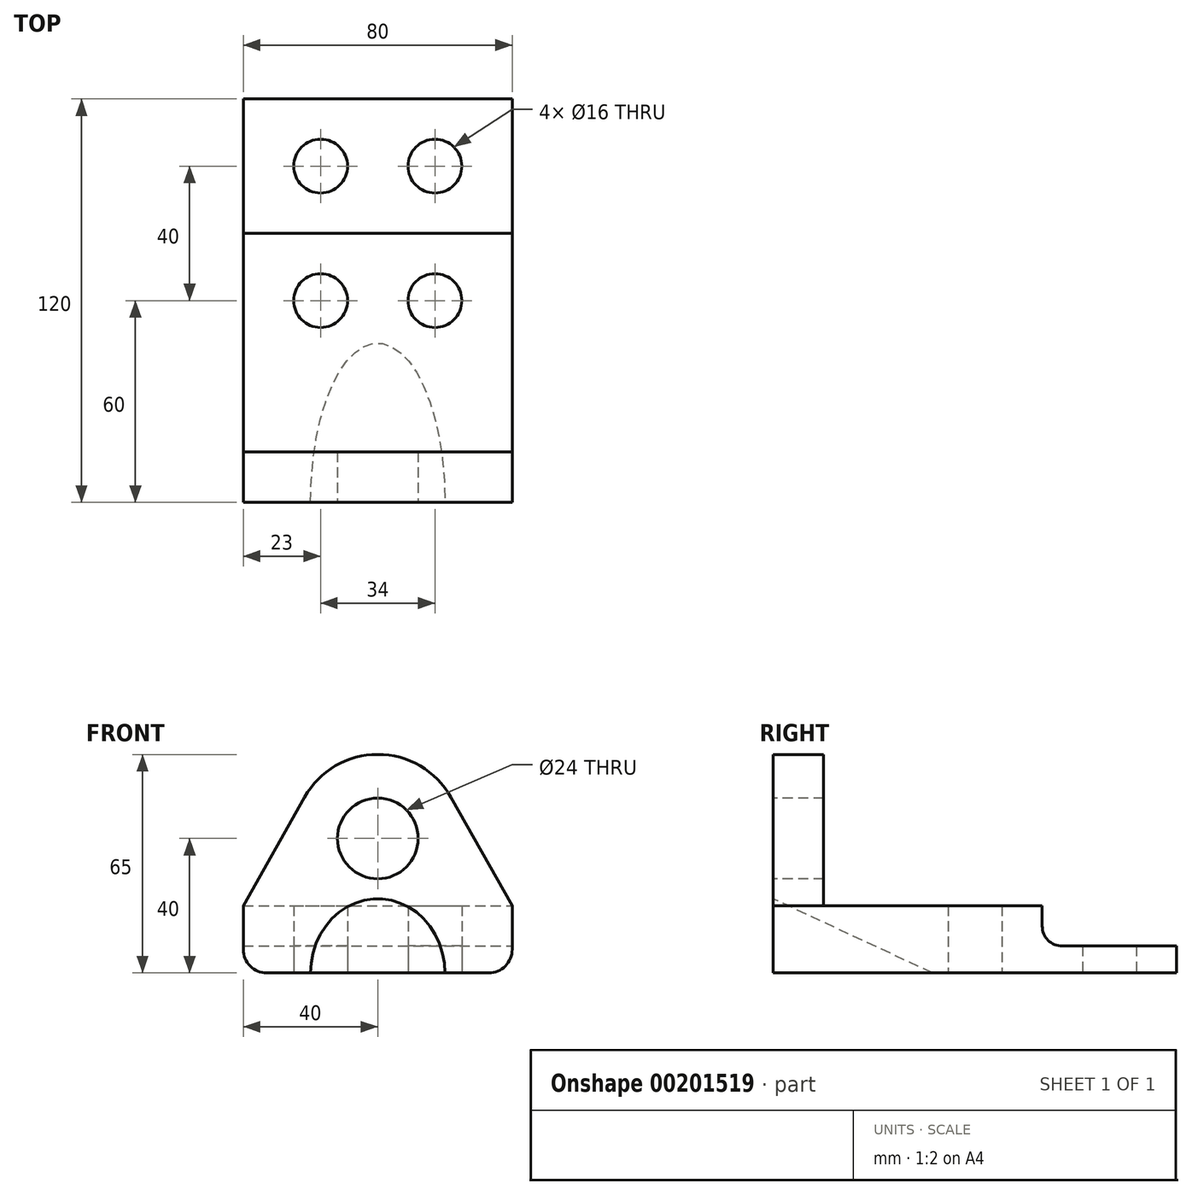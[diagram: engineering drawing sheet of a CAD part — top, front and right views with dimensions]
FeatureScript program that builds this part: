
annotation { "Feature Type Name" : "Feature", "Feature Type Description" : "" }
export const myFeature = defineFeature(function(context is Context, id is Id, definition is map)
    precondition{}
    {
        {
            var Q0;
            Q0=qCreatedBy(makeId("Front.planeOp"),FACE);
            var sketch = newSketch(context, id + "F0", { "sketchPlane" : qUnion([Q0])});
            skArc(sketch, "E0", {"start": v(21.77, 52.3) * mm, "mid": v(0, 65) * mm, "end": v(-21.77, 52.3) * mm});
            skLineSegment(sketch, "E1", {"start": v(-40, 0) * mm, "end": v(40, 0) * mm});
            skLineSegment(sketch, "E2", {"start": v(40, 0) * mm, "end": v(40, 20) * mm});
            skLineSegment(sketch, "E3", {"start": v(40, 20) * mm, "end": v(21.77, 52.3) * mm});
            skLineSegment(sketch, "E4", {"start": v(-40, 0) * mm, "end": v(-40, 20) * mm});
            skLineSegment(sketch, "E5", {"start": v(-40, 20) * mm, "end": v(-21.77, 52.3) * mm});
            skLineSegment(sketch, "E6", {"start": v(-40, 20) * mm, "end": v(40, 20) * mm});
            skCircle(sketch, "E7", {"center": v(0, 40) * mm, "radius": 12 * mm});
            skSolve(sketch);
        }
        {
            var Q0;
            Q0=makeQuery(id+"F0.imprint","IMPRINT",FACE,{"disambiguationData":[TD([[makeQuery(id+"F0.imprint","IMPRINT",EDGE,{"derivedFrom":sQuery(id+"F0.wireOp",EDGE,"E1")}),1.0]])]});
            extrude(context, id + "F1", {"entities" : qUnion([Q0]), "oppositeDirection" : true, "depth" : 120 * mm});
        }
        {
            var Q0;
            Q0=makeQuery(id+"F0.imprint","IMPRINT",FACE,{"disambiguationData":[TD([[makeQuery(id+"F0.imprint","IMPRINT",EDGE,{"derivedFrom":sQuery(id+"F0.wireOp",EDGE,"E0")}),1.0]])]});
            extrude(context, id + "F2", {"entities" : qUnion([Q0]), "operationType" : NewBodyOperationType.ADD, "oppositeDirection" : true, "depth" : 15 * mm});
        }
        {
            var Q0;
            Q0=makeQuery(id+"F1.opExtrude","SWEPT_FACE",FACE,{"disambiguationData":[OSD([sQuery(id+"F0.wireOp",EDGE,"E6")])]});
            var sketch = newSketch(context, id + "F3", { "sketchPlane" : qUnion([Q0])});
            skLineSegment(sketch, "E8.bottom", {"start": v(-40, 120) * mm, "end": v(40, 120) * mm});
            skLineSegment(sketch, "E8.top", {"start": v(-40, 80) * mm, "end": v(40, 80) * mm});
            skLineSegment(sketch, "E8.left", {"start": v(-40, 120) * mm, "end": v(-40, 80) * mm});
            skLineSegment(sketch, "E8.right", {"start": v(40, 120) * mm, "end": v(40, 80) * mm});
            skSolve(sketch);
        }
        {
            var Q0;
            Q0=makeQuery(id+"F3.imprint","IMPRINT",FACE,{"disambiguationData":[TD([[makeQuery(id+"F3.imprint","IMPRINT",EDGE,{"derivedFrom":sQuery(id+"F3.wireOp",EDGE,"E8.bottom")}),-1.0]])]});
            extrude(context, id + "F4", {"entities" : qUnion([Q0]), "operationType" : NewBodyOperationType.REMOVE, "oppositeDirection" : true, "depth" : (20 - 8) * mm});
        }
        {
            var Q0;
            Q0=makeQuery(id+"F4.boolean.opBoolean","COPY",EDGE,{"derivedFrom":makeQuery(id+"F4.opExtrude","CAP_EDGE",EDGE,{"disambiguationData":[OSD([sQuery(id+"F3.wireOp",EDGE,"E8.top")])],"isStart":false})});
            fillet(context, id + "F5", {"entities" : qUnion([Q0]), "radius" : 6 * mm, "tangentPropagation" : true, "allowEdgeOverflow" : false});
        }
        {
            var Q0;
            Q0=makeQuery(id+"F1.opExtrude","SWEPT_EDGE",EDGE,{"disambiguationData":[OSD([sQuery(id+"F0.wireOp",EDGE,"E1"),sQuery(id+"F0.wireOp",EDGE,"E2")])]});
            var Q1;
            Q1=makeQuery(id+"F1.opExtrude","SWEPT_EDGE",EDGE,{"disambiguationData":[OSD([sQuery(id+"F0.wireOp",EDGE,"E1"),sQuery(id+"F0.wireOp",EDGE,"E4")])]});
            fillet(context, id + "F6", {"entities" : qUnion([Q0, Q1]), "radius" : 7 * mm, "tangentPropagation" : true, "allowEdgeOverflow" : false});
        }
        {
            var Q0;
            Q0=makeQuery(id+"F1.opExtrude","SWEPT_FACE",FACE,{"disambiguationData":[OSD([sQuery(id+"F0.wireOp",EDGE,"E1")])]});
            var sketch = newSketch(context, id + "F7", { "sketchPlane" : qUnion([Q0])});
            skLineSegment(sketch, "E9.bottom", {"start": v(17, -60) * mm, "end": v(-17, -60) * mm, "construction": true});
            skLineSegment(sketch, "E9.top", {"start": v(17, -100) * mm, "end": v(-17, -100) * mm, "construction": true});
            skLineSegment(sketch, "E9.left", {"start": v(17, -60) * mm, "end": v(17, -100) * mm, "construction": true});
            skLineSegment(sketch, "E9.right", {"start": v(-17, -60) * mm, "end": v(-17, -100) * mm, "construction": true});
            skCircle(sketch, "E10", {"center": v(17, -60) * mm, "radius": 8 * mm});
            skCircle(sketch, "E11", {"center": v(17, -100) * mm, "radius": 8 * mm});
            skCircle(sketch, "E12", {"center": v(-17, -100) * mm, "radius": 8 * mm});
            skCircle(sketch, "E13", {"center": v(-17, -60) * mm, "radius": 8 * mm});
            skSolve(sketch);
        }
        {
            var Q0;
            Q0=qSketchRegion(id+"F7",true);
            extrude(context, id + "F8", {"entities" : qUnion([Q0]), "operationType" : NewBodyOperationType.REMOVE, "endBound" : BoundingType.UP_TO_NEXT, "oppositeDirection" : true, "depth" : 25 * mm});
        }
        {
            var Q0;
            Q0=sQuery(id+"F0.wireOp",EDGE,"E1");
            cPlane(context, id + "F9", {"entities" : qUnion([Q0]), "cplaneType" : CPlaneType.LINE_ANGLE, "offset" : 25 * mm, "angle" : 155 * degree, "width" : 150 * mm, "height" : 150 * mm});
        }
        {
            var Q0;
            Q0=qCreatedBy(id+"F9.planeOp",FACE);
            var sketch = newSketch(context, id + "F10", { "sketchPlane" : qUnion([Q0])});
            skCircle(sketch, "E14", {"center": v(0, 0) * mm, "radius": 20 * mm});
            skSolve(sketch);
        }
        {
            var Q0;
            Q0=qSketchRegion(id+"F10",true);
            extrude(context, id + "F11", {"entities" : qUnion([Q0]), "operationType" : NewBodyOperationType.REMOVE, "endBound" : BoundingType.THROUGH_ALL, "oppositeDirection" : true, "depth" : 25 * mm, "hasSecondDirection" : true, "secondDirectionBound" : SecondDirectionBoundingType.THROUGH_ALL, "secondDirectionOppositeDirection" : false, "secondDirectionDepth" : 25 * mm});
        }
    });
